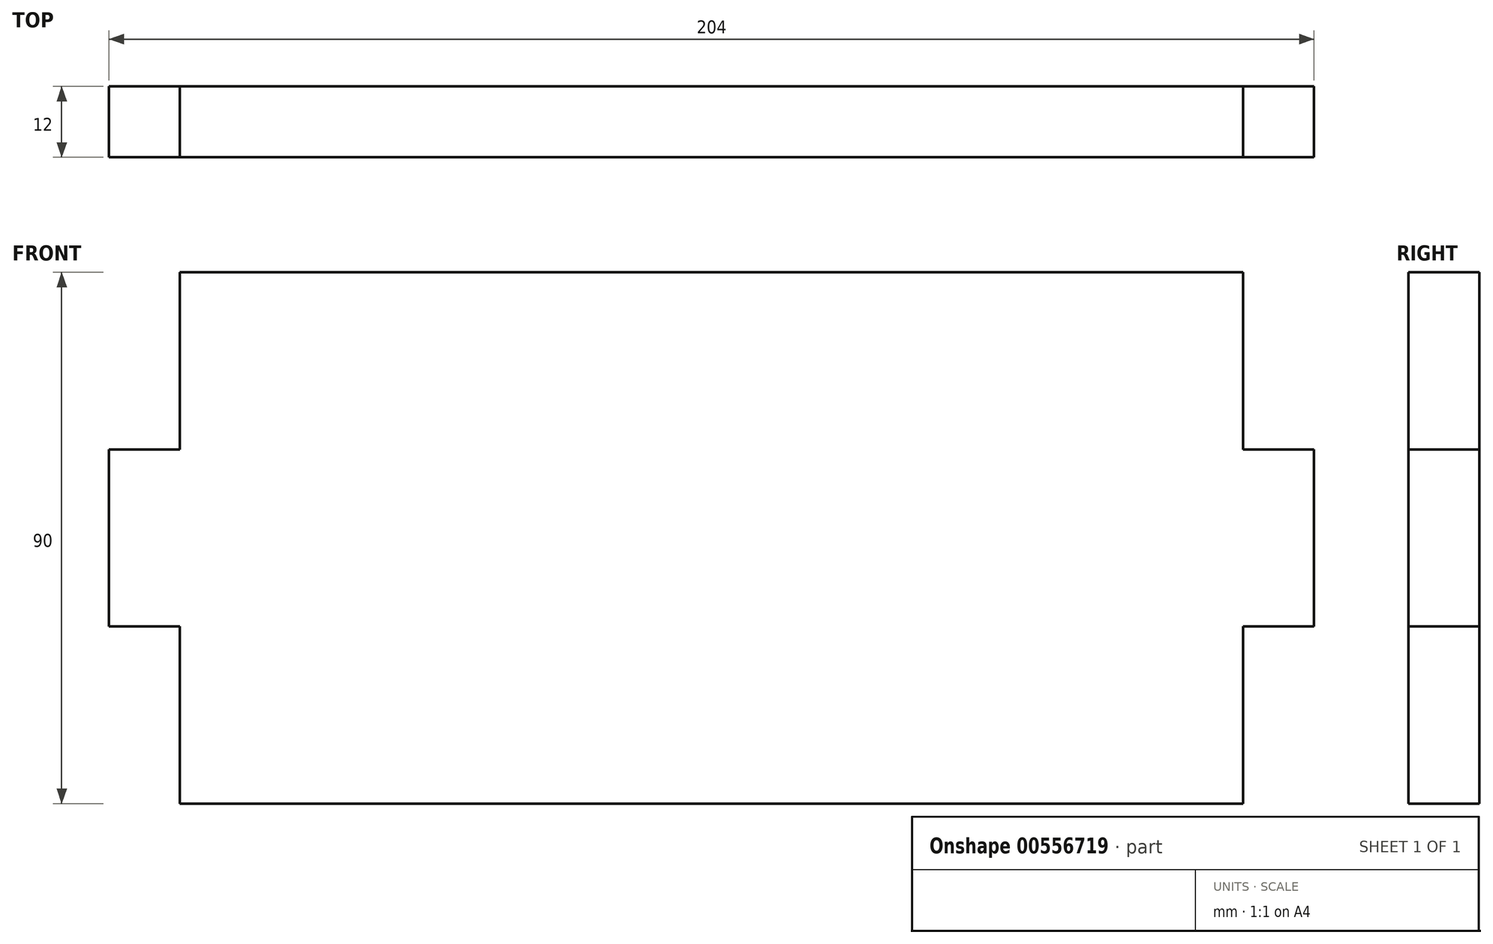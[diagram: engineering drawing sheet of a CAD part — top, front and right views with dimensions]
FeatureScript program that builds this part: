
annotation { "Feature Type Name" : "Feature", "Feature Type Description" : "" }
export const myFeature = defineFeature(function(context is Context, id is Id, definition is map)
    precondition{}
    {
        {
            var Q0;
            Q0=qCreatedBy(makeId("Front.planeOp"),FACE);
            var sketch = newSketch(context, id + "F0", { "sketchPlane" : qUnion([Q0])});
            skLineSegment(sketch, "E0", {"start": v(0, 0) * mm, "end": v(0, 30) * mm});
            skLineSegment(sketch, "E1", {"start": v(0, 30) * mm, "end": v(-12, 30) * mm});
            skLineSegment(sketch, "E2", {"start": v(-12, 30) * mm, "end": v(-12, 60) * mm});
            skLineSegment(sketch, "E3", {"start": v(-12, 60) * mm, "end": v(0, 60) * mm});
            skLineSegment(sketch, "E4", {"start": v(0, 60) * mm, "end": v(0, 90) * mm});
            skLineSegment(sketch, "E5", {"start": v(0, 90) * mm, "end": v(0, 0) * mm});
            skLineSegment(sketch, "E6", {"start": v(90, 0) * mm, "end": v(0, 0) * mm});
            skLineSegment(sketch, "E7", {"start": v(0, 90) * mm, "end": v(90, 90) * mm});
            skLineSegment(sketch, "E8", {"start": v(90, 90) * mm, "end": v(90, 0) * mm, "construction": true});
            skLineSegment(sketch, "E9.MirrorCS", {"start": v(180, 30) * mm, "end": v(192, 30) * mm});
            skLineSegment(sketch, "E10.MirrorCS", {"start": v(192, 60) * mm, "end": v(180, 60) * mm});
            skLineSegment(sketch, "E11.MirrorCS", {"start": v(192, 30) * mm, "end": v(192, 60) * mm});
            skLineSegment(sketch, "E12.MirrorCS", {"start": v(180, 60) * mm, "end": v(180, 90) * mm});
            skLineSegment(sketch, "E13.MirrorCS", {"start": v(180, 0) * mm, "end": v(180, 30) * mm});
            skLineSegment(sketch, "E14.MirrorCS", {"start": v(90, 0) * mm, "end": v(180, 0) * mm});
            skLineSegment(sketch, "E15.MirrorCS", {"start": v(180, 90) * mm, "end": v(90, 90) * mm});
            skLineSegment(sketch, "E16.MirrorCS", {"start": v(180, 90) * mm, "end": v(180, 0) * mm});
            skSolve(sketch);
        }
        {
            var Q0;
            Q0 = qSketchRegion(id + "F0", true);
            extrude(context, id + "F1", {"entities" : qUnion([Q0]), "endBound" : BoundingType.SYMMETRIC, "depth" : 12 * mm, "offsetDistance" : 25 * mm});
        }
    });
